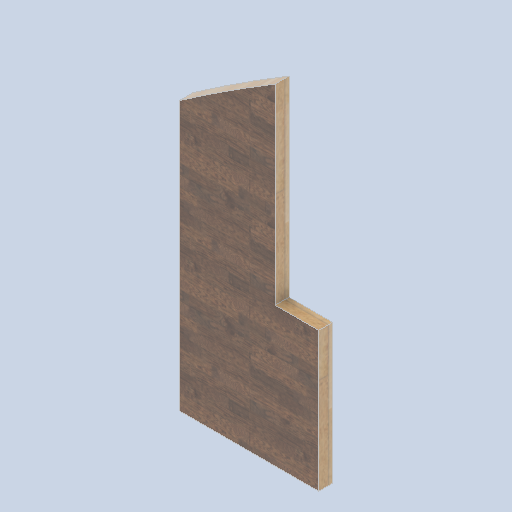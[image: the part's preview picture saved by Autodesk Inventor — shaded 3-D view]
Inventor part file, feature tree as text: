
AUTODESK INVENTOR PART (.ipt)
format: ipt  version: 2024.2 (Build 282272000, 272)  size: 175,104 bytes
history: native  units: in
note: dims shown in document units (in); Inventor stores cm internally (conversion verified against a paired STEP export)
features: other x3, sketch x1
ambient origin geometry x8: Origin, YZ Plane, XZ Plane, XY Plane, X Axis, Y Axis, Z Axis, Center Point
bodies: Solid1 (feature_tree)
feature tree (4):
  other  "front_wall_block03.ipt"
  other  "Solid1::front_wall_block03.ipt"
  other  "TaggingFeature1"
  sketch  "Sketch1"  dims[d0=0.3937in]
